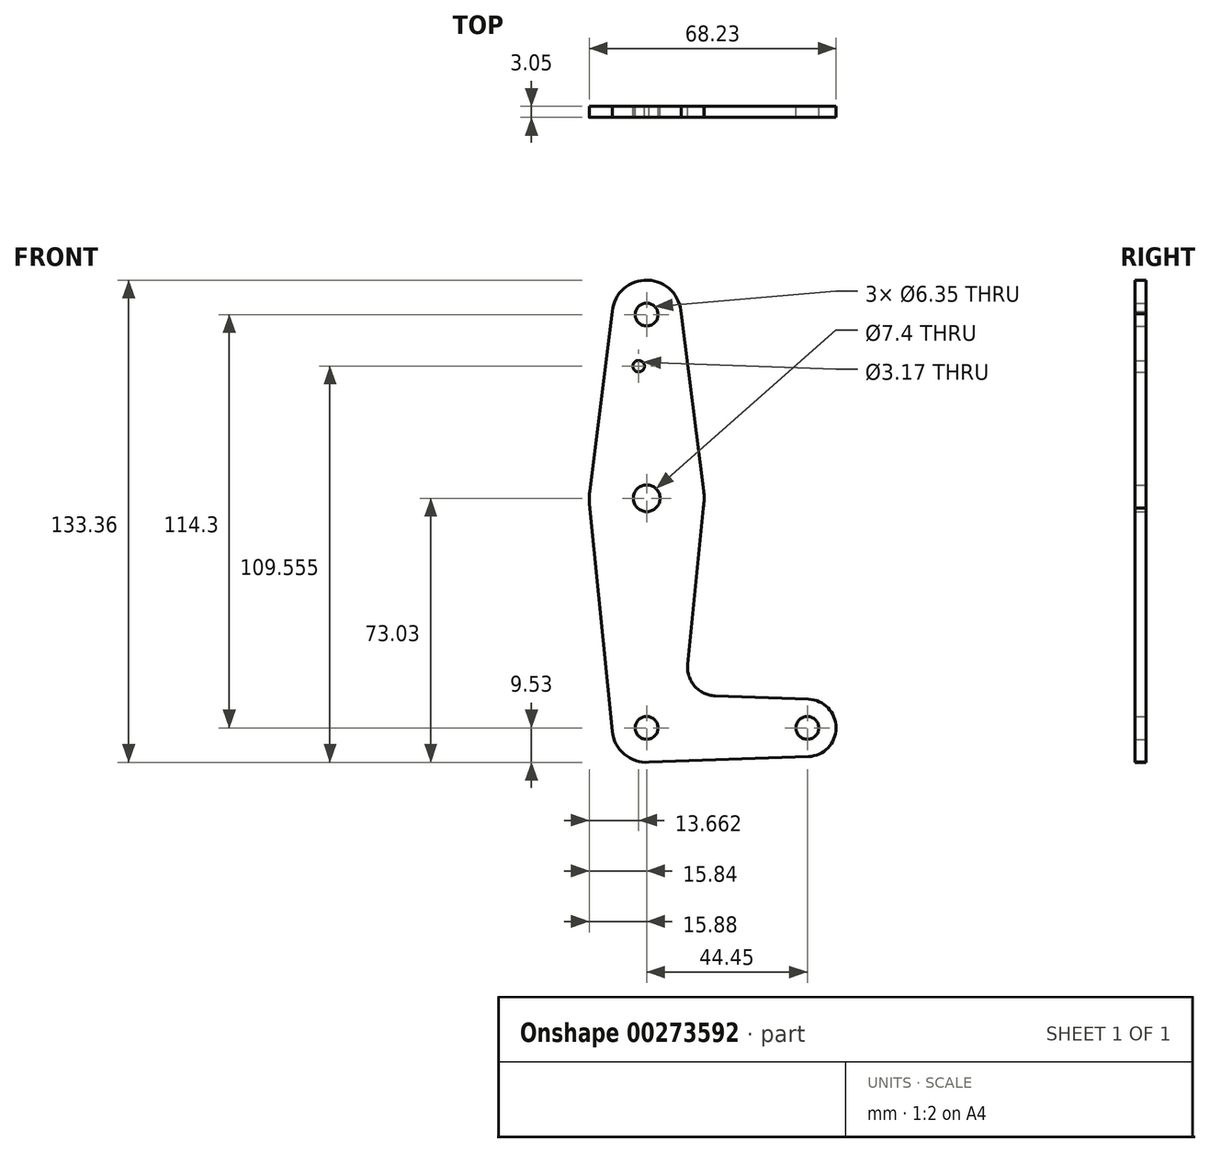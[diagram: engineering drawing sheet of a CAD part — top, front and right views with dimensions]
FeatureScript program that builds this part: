
annotation { "Feature Type Name" : "Feature", "Feature Type Description" : "" }
export const myFeature = defineFeature(function(context is Context, id is Id, definition is map)
    precondition{}
    {
        {
            var Q0;
            Q0=qCreatedBy(makeId("Front.planeOp"),FACE);
            var sketch = newSketch(context, id + "F0", { "sketchPlane" : qUnion([Q0])});
            skCircle(sketch, "E0", {"center": v(0, 0) * mm, "radius": 9.53 * mm});
            skCircle(sketch, "E1", {"center": v(44.45, 0) * mm, "radius": 7.94 * mm});
            skCircle(sketch, "E2", {"center": v(0.04, 63.5) * mm, "radius": 15.88 * mm});
            skCircle(sketch, "E3", {"center": v(0, 114.3) * mm, "radius": 9.53 * mm});
            skCircle(sketch, "E4", {"center": v(0.04, 63.5) * mm, "radius": 3.7 * mm});
            skCircle(sketch, "E5", {"center": v(0, 0) * mm, "radius": 3.18 * mm});
            skCircle(sketch, "E6", {"center": v(44.45, 0) * mm, "radius": 3.18 * mm});
            skCircle(sketch, "E7", {"center": v(0, 114.3) * mm, "radius": 3.18 * mm});
            skLineSegment(sketch, "E8", {"start": v(0, -9.53) * mm, "end": v(44.73, -7.93) * mm});
            skCircle(sketch, "E9", {"center": v(-2.18, 100.03) * mm, "radius": 1.59 * mm});
            skLineSegment(sketch, "E10", {"start": v(18.97, 8.85) * mm, "end": v(44.73, 7.93) * mm});
            skArc(sketch, "E11.filletArc", {"start": v(11.34, 17.59) * mm, "mid": v(13.26, 11.57) * mm, "end": v(18.97, 8.85) * mm});
            skLineSegment(sketch, "E12", {"start": v(9.52, 114.5) * mm, "end": v(15.79, 65.5) * mm});
            skLineSegment(sketch, "E13", {"start": v(15.75, 61.5) * mm, "end": v(11.34, 17.59) * mm});
            skLineSegment(sketch, "E14", {"start": v(-9.48, 115.19) * mm, "end": v(-15.71, 65.47) * mm});
            skLineSegment(sketch, "E15", {"start": v(0.04, 63.5) * mm, "end": v(0, 0) * mm});
            skLineSegment(sketch, "E16", {"start": v(0, 114.3) * mm, "end": v(0, 63.5) * mm});
            skLineSegment(sketch, "E17", {"start": v(-15.76, 61.92) * mm, "end": v(-9.48, -0.95) * mm});
            skSolve(sketch);
        }
        {
            var Q0;
            Q0 = qSketchRegion(id + "F0", true);
            extrude(context, id + "F1", {"entities" : qUnion([Q0]), "depth" : 3.05 * mm});
        }
    });
